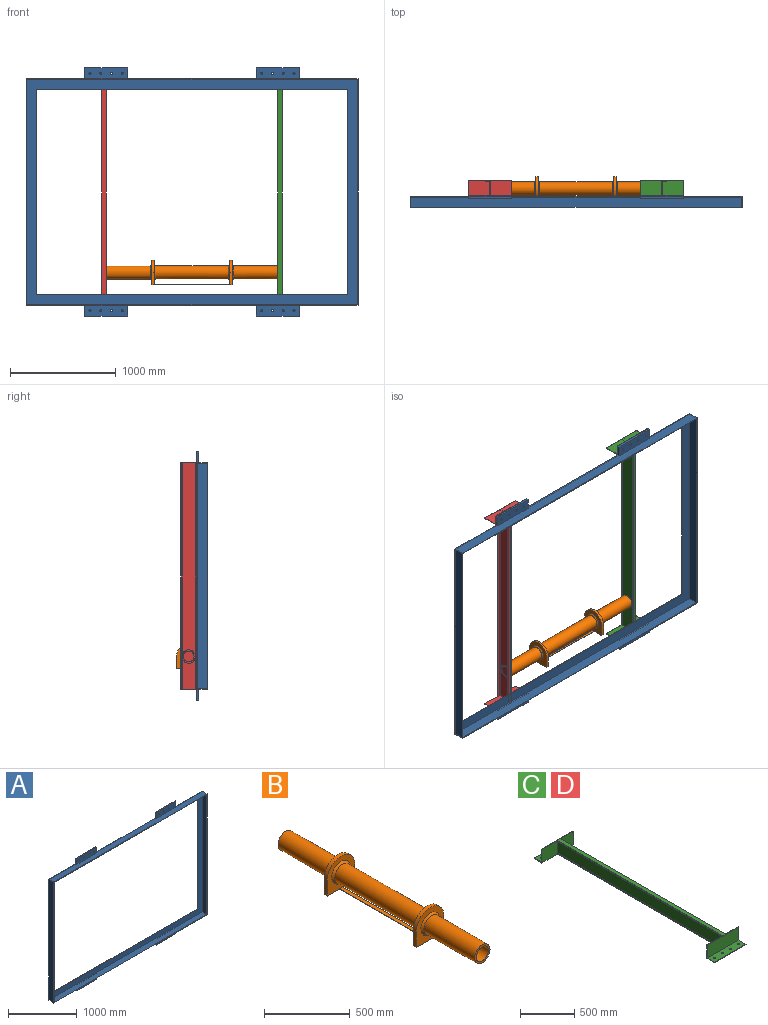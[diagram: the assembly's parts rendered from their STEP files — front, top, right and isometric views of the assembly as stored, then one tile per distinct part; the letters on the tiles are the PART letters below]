
ASSEMBLY  parts=4 mates=3
PART A: 47 faces, bbox 3141.6x101.6x2347.9 mm
  f0: plane 3141.64x2347.89mm, normal (0,1,0), area 1193493mm2, adj f4,f6,f7,f9,f10,f12,f13,f17
  f1: plane 406.4x101.6mm, normal (0,-1,0), area 40150.1mm2, adj f10,f22,f23,f24,f39,f40,f41,f42
  f2: plane 406.4x101.6mm, normal (0,-1,0), area 40150.1mm2, adj f7,f25,f26,f27,f35,f36,f37,f38
  f3: plane 406.4x101.6mm, normal (0,-1,0), area 40150.1mm2, adj f7,f28,f29,f30,f31,f32,f33,f34
  f4: plane 2144.69x101.6mm, normal (-1,0,0), area 217900.6mm2, adj f0,f7,f10,f14
  f5: plane 2131.99x95.25mm, normal (1,0,0), area 203072.1mm2, adj f8,f11,f14,f16
  f6: plane 1941.49x6.35mm, normal (1,0,0), area 12328.5mm2, adj f0,f9,f12,f16
  f7: plane 3141.64x101.6mm, normal (0,0,-1), area 303706.9mm2, adj f0,f2,f3,f4,f13,f14,f25,f27
  f8: plane 3128.94x95.25mm, normal (0,0,1), area 298031.6mm2, adj f5,f14,f15,f16
  f9: plane 2938.44x6.35mm, normal (0,0,1), area 18659.1mm2, adj f0,f6,f16,f17
  f10: plane 3141.64x101.6mm, normal (0,0,1), area 303706.9mm2, adj f0,f1,f4,f13,f14,f19,f20,f21
  f11: plane 3128.94x95.25mm, normal (0,0,-1), area 298031.6mm2, adj f5,f14,f15,f16
  f12: plane 2938.44x6.35mm, normal (0,0,-1), area 18659.1mm2, adj f0,f6,f16,f17
  f13: plane 2144.69x101.6mm, normal (1,0,0), area 217900.6mm2, adj f0,f7,f10,f14
  f14: plane 3141.64x2144.69mm, normal (0,-1,0), area 66975.1mm2, adj f4,f5,f7,f8,f10,f11,f13,f15
  f15: plane 2131.99x95.25mm, normal (-1,0,0), area 203072.1mm2, adj f8,f11,f14,f16
  f16: plane 3128.94x2131.99mm, normal (0,-1,0), area 965917.3mm2, adj f5,f6,f8,f9,f11,f12,f15,f17
  f17: plane 1941.49x6.35mm, normal (-1,0,0), area 12328.5mm2, adj f0,f9,f12,f16
  f18: plane 406.4x19.05mm, normal (0,0,1), area 7741.9mm2, adj f0,f19,f20,f21
  f19: plane 101.6x19.05mm, normal (1,0,0), area 1935.5mm2, adj f0,f10,f18,f21
  f20: plane 101.6x19.05mm, normal (-1,0,0), area 1935.5mm2, adj f0,f10,f18,f21
  f21: plane 406.4x101.6mm, normal (0,-1,0), area 40150.1mm2, adj f10,f18,f19,f20,f43,f44,f45,f46
  f22: plane 406.4x19.05mm, normal (0,0,1), area 7741.9mm2, adj f0,f1,f23,f24
  f23: plane 101.6x19.05mm, normal (1,0,0), area 1935.5mm2, adj f0,f1,f10,f22
  f24: plane 101.6x19.05mm, normal (-1,0,0), area 1935.5mm2, adj f0,f1,f10,f22
  f25: plane 101.6x19.05mm, normal (1,0,0), area 1935.5mm2, adj f0,f2,f7,f26
  f26: plane 406.4x19.05mm, normal (0,0,-1), area 7741.9mm2, adj f0,f2,f25,f27
  f27: plane 101.6x19.05mm, normal (-1,0,0), area 1935.5mm2, adj f0,f2,f7,f26
  f28: plane 406.4x19.05mm, normal (0,0,-1), area 7741.9mm2, adj f0,f3,f29,f30
  f29: plane 101.6x19.05mm, normal (-1,0,0), area 1935.5mm2, adj f0,f3,f7,f28
  f30: plane 101.6x19.05mm, normal (1,0,0), area 1935.5mm2, adj f0,f3,f7,f28
  f31: cylinder r=9.53mm len=19.05mm, axis (0,1,0), area 1140.1mm2, adj f0,f3
  f32: cylinder r=9.53mm len=19.05mm, axis (0,1,0), area 1140.1mm2, adj f0,f3
  f33: cylinder r=9.53mm len=19.05mm, axis (0,1,0), area 1140.1mm2, adj f0,f3
  f34: cylinder r=9.53mm len=19.05mm, axis (0,1,0), area 1140.1mm2, adj f0,f3
  f35: cylinder r=9.53mm len=19.05mm, axis (0,1,0), area 1140.1mm2, adj f0,f2
  f36: cylinder r=9.53mm len=19.05mm, axis (0,1,0), area 1140.1mm2, adj f0,f2
  f37: cylinder r=9.53mm len=19.05mm, axis (0,1,0), area 1140.1mm2, adj f0,f2
  f38: cylinder r=9.53mm len=19.05mm, axis (0,1,0), area 1140.1mm2, adj f0,f2
  f39: cylinder r=9.53mm len=19.05mm, axis (0,1,0), area 1140.1mm2, adj f0,f1
  f40: cylinder r=9.53mm len=19.05mm, axis (0,1,0), area 1140.1mm2, adj f0,f1
  f41: cylinder r=9.53mm len=19.05mm, axis (0,1,0), area 1140.1mm2, adj f0,f1
  f42: cylinder r=9.53mm len=19.05mm, axis (0,1,0), area 1140.1mm2, adj f0,f1
  f43: cylinder r=9.53mm len=19.05mm, axis (0,1,0), area 1140.1mm2, adj f0,f21
  f44: cylinder r=9.53mm len=19.05mm, axis (0,1,0), area 1140.1mm2, adj f0,f21
  f45: cylinder r=9.53mm len=19.05mm, axis (0,1,0), area 1140.1mm2, adj f0,f21
  f46: cylinder r=9.53mm len=19.05mm, axis (0,1,0), area 1140.1mm2, adj f0,f21
PART B: 25 faces, bbox 228.6x1625.6x228.6 mm
  f0: plane 228.6x228.6mm, normal (0,1,0), area 28344.6mm2, adj f7,f8,f9,f10,f20,f22,f23,f24
  f1: plane 228.6x228.6mm, normal (0,-1,0), area 28344.6mm2, adj f10,f12,f13,f14,f19,f22,f23,f24
  f2: cylinder r=63.5mm len=685.8mm, axis (0,1,0), area 273622mm2, adj f19,f20
  f3: cylinder r=63.5mm len=419.1mm, axis (0,1,0), area 167213.5mm2, adj f4,f18
  f4: plane 127x127mm, normal (0,-1,0), area 4560.4mm2, adj f3,f5
  f5: cylinder r=50.8mm len=1612.9mm, axis (0,1,0), area 514814.8mm2, adj f4,f6
  f6: plane 101.6x101.6mm, normal (0,-1,0), area 8107.3mm2, adj f5
  f7: plane 114.3x25.4mm, normal (1,0,0), area 2903.2mm2, adj f0,f8,f10,f11
  f8: cylinder r=114.3mm len=228.6mm, axis (0,-1,0), area 9120.7mm2, adj f0,f7,f9,f11
  f9: plane 114.3x25.4mm, normal (-1,0,0), area 2903.2mm2, adj f0,f8,f10,f11
  f10: plane 762x228.6mm, normal (0,0,-1), area 29677.4mm2, adj f0,f1,f7,f9,f11,f12,f13,f15
  f11: plane 228.6x228.6mm, normal (0,-1,0), area 28409.2mm2, adj f7,f8,f9,f10,f18
  f12: plane 114.3x25.4mm, normal (1,0,0), area 2903.2mm2, adj f1,f10,f14,f15
  f13: plane 114.3x25.4mm, normal (-1,0,0), area 2903.2mm2, adj f1,f10,f14,f15
  f14: cylinder r=114.3mm len=228.6mm, axis (0,1,0), area 9120.7mm2, adj f1,f12,f13,f15
  f15: plane 228.6x228.6mm, normal (0,1,0), area 28409.2mm2, adj f10,f12,f13,f14,f21
  f16: plane 127x127mm, normal (0,1,0), area 12667.7mm2, adj f17
  f17: cylinder r=63.5mm len=419.1mm, axis (0,1,0), area 167213.5mm2, adj f16,f21
  f18: cone r=63.5mm half-angle=45deg, axis (0,1,0), area 7882.5mm2, adj f3,f11
  f19: cone r=76.2mm half-angle=45deg, axis (0,1,0), area 7882.5mm2, adj f1,f2
  f20: cone r=76.2mm half-angle=45deg, axis (0,-1,0), area 7882.5mm2, adj f0,f2
  f21: cone r=76.2mm half-angle=45deg, axis (0,-1,0), area 7882.5mm2, adj f15,f17
  f22: plane 711.2x2.54mm, normal (1,0,0), area 1806.4mm2, adj f0,f1,f10,f24
  f23: plane 711.2x2.54mm, normal (-1,0,0), area 1806.4mm2, adj f0,f1,f10,f24
  f24: plane 711.2x25.4mm, normal (0,0,1), area 18064.5mm2, adj f0,f1,f22,f23
PART C: 32 faces, bbox 406.4x2347.9x152.4 mm
  f0: plane 2347.87x406.4mm, normal (0,0,-1), area 166955.3mm2, adj f5,f6,f10,f11,f14,f15,f16,f17
  f1: cylinder r=6.35mm len=2144.67mm, axis (0,1,0), area 21392.2mm2, adj f2,f9,f11,f18
  f2: plane 2144.67x29.21mm, normal (0,0,-1), area 62645.9mm2, adj f1,f3,f11,f18
  f3: plane 2144.67x7.52mm, normal (1,0,0), area 16124.5mm2, adj f2,f4,f11,f18
  f4: plane 2157.37x406.4mm, normal (0,0,1), area 91449.3mm2, adj f3,f5,f10,f11,f12,f15,f16,f17
  f5: plane 2144.67x152.4mm, normal (-1,0,0), area 326848.4mm2, adj f0,f4,f10,f17
  f6: plane 2144.67x7.52mm, normal (1,0,0), area 16124.5mm2, adj f0,f7,f11,f18
  f7: plane 2144.67x29.21mm, normal (0,0,1), area 62645.9mm2, adj f6,f8,f11,f18
  f8: cylinder r=6.35mm len=2144.67mm, axis (0,1,0), area 21392.2mm2, adj f7,f9,f11,f18
  f9: plane 2144.67x124.66mm, normal (1,0,0), area 267362mm2, adj f1,f8,f11,f18
  f10: plane 203.2x152.4mm, normal (0,-1,0), area 30967.7mm2, adj f0,f4,f5,f15
  f11: plane 198.53x152.4mm, normal (0,-1,0), area 29703.4mm2, adj f0,f1,f2,f3,f4,f6,f7,f8
  f12: plane 406.4x146.05mm, normal (0,1,0), area 59354.7mm2, adj f4,f13,f15,f16
  f13: plane 406.4x95.25mm, normal (0,0,1), area 37753mm2, adj f12,f14,f15,f16,f28,f29,f30,f31
  f14: plane 406.4x6.35mm, normal (0,1,0), area 2580.6mm2, adj f0,f13,f15,f16
  f15: plane 152.4x101.6mm, normal (-1,0,0), area 1572.6mm2, adj f0,f4,f10,f12,f13,f14
  f16: plane 152.4x101.6mm, normal (1,0,0), area 1572.6mm2, adj f0,f4,f11,f12,f13,f14
  f17: plane 203.2x152.4mm, normal (0,1,0), area 30967.7mm2, adj f0,f4,f5,f22
  f18: plane 198.53x152.4mm, normal (0,1,0), area 29703.4mm2, adj f0,f1,f2,f3,f4,f6,f7,f8
  f19: plane 406.4x6.35mm, normal (0,-1,0), area 2580.6mm2, adj f0,f20,f22,f23
  f20: plane 406.4x95.25mm, normal (0,0,1), area 37753mm2, adj f19,f21,f22,f23,f24,f25,f26,f27
  f21: plane 406.4x146.05mm, normal (0,-1,0), area 59354.7mm2, adj f4,f20,f22,f23
  f22: plane 152.4x101.6mm, normal (-1,0,0), area 1572.6mm2, adj f0,f4,f17,f19,f20,f21
  f23: plane 152.4x101.6mm, normal (1,0,0), area 1572.6mm2, adj f0,f4,f18,f19,f20,f21
  f24: cylinder r=8.72mm len=17.45mm, axis (0,0,-1), area 348.1mm2, adj f0,f20
  f25: cylinder r=8.72mm len=17.45mm, axis (0,0,-1), area 348.1mm2, adj f0,f20
  f26: cylinder r=8.72mm len=17.45mm, axis (0,0,-1), area 348.1mm2, adj f0,f20
  f27: cylinder r=8.72mm len=17.45mm, axis (0,0,-1), area 348.1mm2, adj f0,f20
  f28: cylinder r=8.72mm len=17.45mm, axis (0,0,-1), area 348.1mm2, adj f0,f13
  f29: cylinder r=8.72mm len=17.45mm, axis (0,0,-1), area 348.1mm2, adj f0,f13
  f30: cylinder r=8.72mm len=17.45mm, axis (0,0,-1), area 348.1mm2, adj f0,f13
  f31: cylinder r=8.72mm len=17.45mm, axis (0,0,-1), area 348.1mm2, adj f0,f13
PART D: same geometry as C
PLACE A t=(-904.67,-914.58,-1429)mm
PLACE B rot(axis=(0,0,-1),90deg) t=(-898.36,-838.38,-2558.34)mm
PLACE C rot(axis=(-1,0,0),90deg) t=(-66.99,-861.12,-1796.34)mm
PLACE D rot(axis=(0,-0.71,-0.71),180deg) t=(-1729.74,-861.12,-1796.34)mm
MATE fastened D.f5 <-> B.f2  axis (1,0,0) through (-1711.16,-838.38,-2558.34)mm
MATE fastened B.f2 <-> C.f5  axis (1,0,0) through (-85.56,-838.38,-2558.34)mm
MATE fastened A.f44 <-> C.f25  axis (0,1,0) through (66.84,-914.58,-673.2)mm
